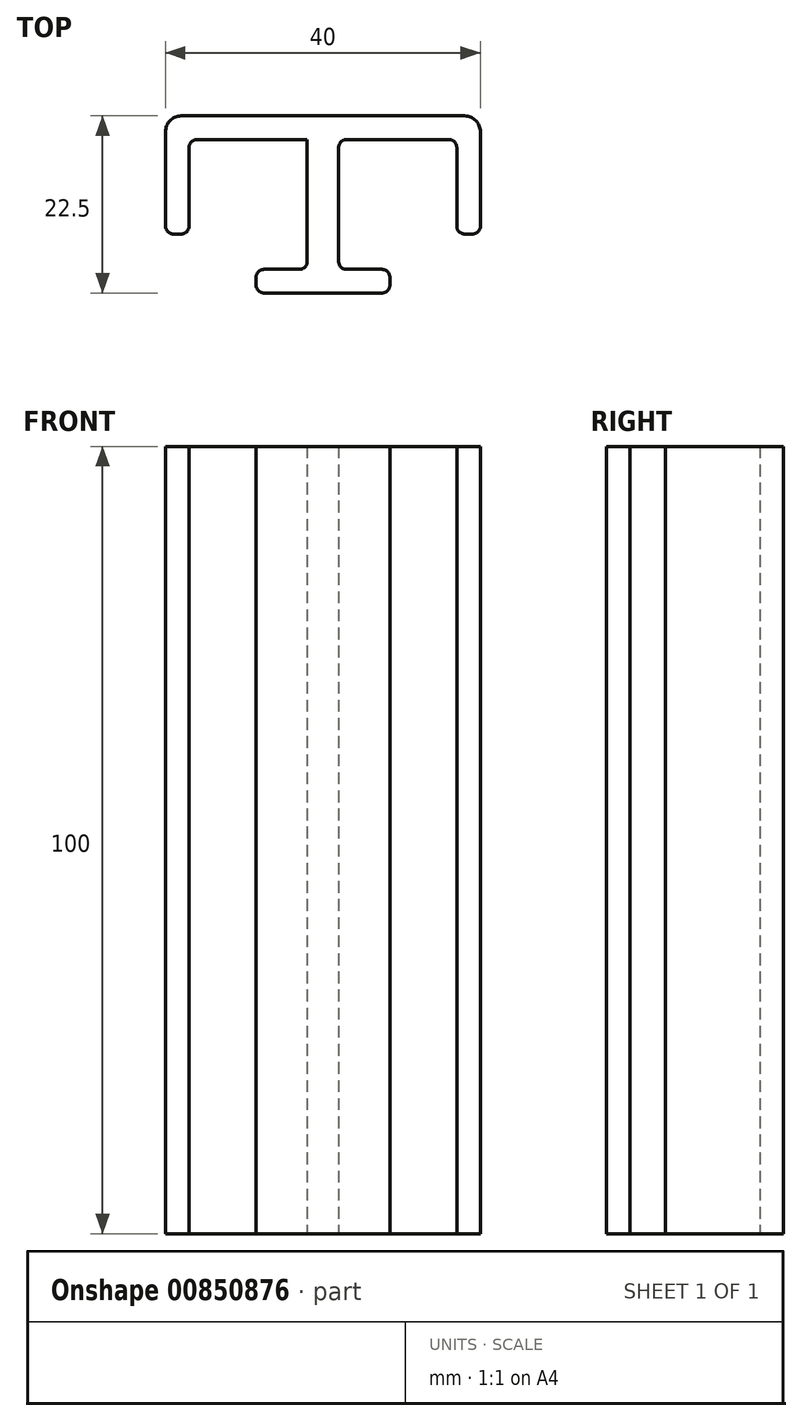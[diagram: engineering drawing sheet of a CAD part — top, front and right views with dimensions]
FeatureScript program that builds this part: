
annotation { "Feature Type Name" : "Feature", "Feature Type Description" : "" }
export const myFeature = defineFeature(function(context is Context, id is Id, definition is map)
    precondition{}
    {
        {
            var Q0;
            Q0=qCreatedBy(makeId("Top.planeOp"),FACE);
            var sketch = newSketch(context, id + "F0", { "sketchPlane" : qUnion([Q0])});
            skLineSegment(sketch, "E0", {"start": v(-20, 10) * mm, "end": v(20, 10) * mm});
            skLineSegment(sketch, "E1", {"start": v(20, 10) * mm, "end": v(20, -5) * mm});
            skLineSegment(sketch, "E2", {"start": v(-20, 10) * mm, "end": v(-20, -5) * mm});
            skLineSegment(sketch, "E3.0", {"start": v(-17, 7) * mm, "end": v(-17, -5) * mm});
            skLineSegment(sketch, "E3.1", {"start": v(-17, 7) * mm, "end": v(-2, 7) * mm});
            skLineSegment(sketch, "E3.2", {"start": v(17, 7) * mm, "end": v(17, -5) * mm});
            skLineSegment(sketch, "E4", {"start": v(-20, -5) * mm, "end": v(-17, -5) * mm});
            skLineSegment(sketch, "E5", {"start": v(17, -5) * mm, "end": v(20, -5) * mm});
            skLineSegment(sketch, "E6", {"start": v(-2, 7) * mm, "end": v(-2, -9.5) * mm});
            skLineSegment(sketch, "E7", {"start": v(-2, -9.5) * mm, "end": v(-8.5, -9.5) * mm});
            skLineSegment(sketch, "E8", {"start": v(-8.5, -9.5) * mm, "end": v(-8.5, -12.5) * mm});
            skLineSegment(sketch, "E9", {"start": v(-8.5, -12.5) * mm, "end": v(0, -12.5) * mm});
            skLineSegment(sketch, "E10.MirrorCS", {"start": v(2, 7) * mm, "end": v(2, -9.5) * mm});
            skLineSegment(sketch, "E11.MirrorCS", {"start": v(8.5, -12.5) * mm, "end": v(0, -12.5) * mm});
            skLineSegment(sketch, "E12.MirrorCS", {"start": v(2, -9.5) * mm, "end": v(8.5, -9.5) * mm});
            skLineSegment(sketch, "E13.MirrorCS", {"start": v(8.5, -9.5) * mm, "end": v(8.5, -12.5) * mm});
            skLineSegment(sketch, "E14.trimOffspring", {"start": v(2, 7) * mm, "end": v(17, 7) * mm});
            skSolve(sketch);
        }
        {
            var Q0;
            Q0=qSketchRegion(id+"F0",true);
            extrude(context, id + "F1", {"entities" : qUnion([Q0]), "depth" : 100 * mm, "offsetDistance" : 25 * mm});
        }
        {
            var Q0;
            Q0=makeQuery(id+"F1.opExtrude","SWEPT_EDGE",EDGE,{"disambiguationData":[OSD([sQuery(id+"F0.wireOp",EDGE,"E0"),sQuery(id+"F0.wireOp",EDGE,"E2")])]});
            var Q1;
            Q1=makeQuery(id+"F1.opExtrude","SWEPT_EDGE",EDGE,{"disambiguationData":[OSD([sQuery(id+"F0.wireOp",EDGE,"E0"),sQuery(id+"F0.wireOp",EDGE,"E1")])]});
            fillet(context, id + "F2", {"entities" : qUnion([Q0, Q1]), "radius" : 2 * mm, "tangentPropagation" : true, "allowEdgeOverflow" : false});
        }
        {
            var Q0;
            Q0=makeQuery(id+"F1.opExtrude","SWEPT_EDGE",EDGE,{"disambiguationData":[OSD([sQuery(id+"F0.wireOp",EDGE,"E3.0"),sQuery(id+"F0.wireOp",EDGE,"E4")])]});
            var Q1;
            Q1=makeQuery(id+"F1.opExtrude","SWEPT_EDGE",EDGE,{"disambiguationData":[OSD([sQuery(id+"F0.wireOp",EDGE,"E2"),sQuery(id+"F0.wireOp",EDGE,"E4")])]});
            var Q2;
            Q2=makeQuery(id+"F1.opExtrude","SWEPT_EDGE",EDGE,{"disambiguationData":[OSD([sQuery(id+"F0.wireOp",EDGE,"E3.0"),sQuery(id+"F0.wireOp",EDGE,"E3.1")])]});
            var Q3;
            Q3=makeQuery(id+"F1.opExtrude","SWEPT_EDGE",EDGE,{"disambiguationData":[OSD([sQuery(id+"F0.wireOp",EDGE,"E10.MirrorCS"),sQuery(id+"F0.wireOp",EDGE,"E14.trimOffspring")])]});
            var Q4;
            Q4=makeQuery(id+"F1.opExtrude","SWEPT_EDGE",EDGE,{"disambiguationData":[OSD([sQuery(id+"F0.wireOp",EDGE,"E11.MirrorCS"),sQuery(id+"F0.wireOp",EDGE,"E13.MirrorCS")])]});
            var Q5;
            Q5=makeQuery(id+"F1.opExtrude","SWEPT_EDGE",EDGE,{"disambiguationData":[OSD([sQuery(id+"F0.wireOp",EDGE,"E12.MirrorCS"),sQuery(id+"F0.wireOp",EDGE,"E13.MirrorCS")])]});
            var Q6;
            Q6=makeQuery(id+"F1.opExtrude","SWEPT_EDGE",EDGE,{"disambiguationData":[OSD([sQuery(id+"F0.wireOp",EDGE,"E8"),sQuery(id+"F0.wireOp",EDGE,"E9")])]});
            var Q7;
            Q7=makeQuery(id+"F1.opExtrude","SWEPT_EDGE",EDGE,{"disambiguationData":[OSD([sQuery(id+"F0.wireOp",EDGE,"E7"),sQuery(id+"F0.wireOp",EDGE,"E8")])]});
            var Q8;
            Q8=makeQuery(id+"F1.opExtrude","SWEPT_EDGE",EDGE,{"disambiguationData":[OSD([sQuery(id+"F0.wireOp",EDGE,"E6"),sQuery(id+"F0.wireOp",EDGE,"E7")])]});
            var Q9;
            Q9=makeQuery(id+"F1.opExtrude","SWEPT_EDGE",EDGE,{"disambiguationData":[OSD([sQuery(id+"F0.wireOp",EDGE,"E10.MirrorCS"),sQuery(id+"F0.wireOp",EDGE,"E12.MirrorCS")])]});
            var Q10;
            Q10=makeQuery(id+"F1.opExtrude","SWEPT_EDGE",EDGE,{"disambiguationData":[OSD([sQuery(id+"F0.wireOp",EDGE,"E3.2"),sQuery(id+"F0.wireOp",EDGE,"E5")])]});
            var Q11;
            Q11=makeQuery(id+"F1.opExtrude","SWEPT_EDGE",EDGE,{"disambiguationData":[OSD([sQuery(id+"F0.wireOp",EDGE,"E1"),sQuery(id+"F0.wireOp",EDGE,"E5")])]});
            var Q12;
            Q12=makeQuery(id+"F1.opExtrude","SWEPT_EDGE",EDGE,{"disambiguationData":[OSD([sQuery(id+"F0.wireOp",EDGE,"E3.2"),sQuery(id+"F0.wireOp",EDGE,"E14.trimOffspring")])]});
            fillet(context, id + "F3", {"entities" : qUnion([Q0, Q1, Q2, Q3, Q4, Q5, Q6, Q7, Q8, Q9, Q10, Q11, Q12]), "radius" : 1 * mm, "tangentPropagation" : true, "allowEdgeOverflow" : false});
        }
    });
